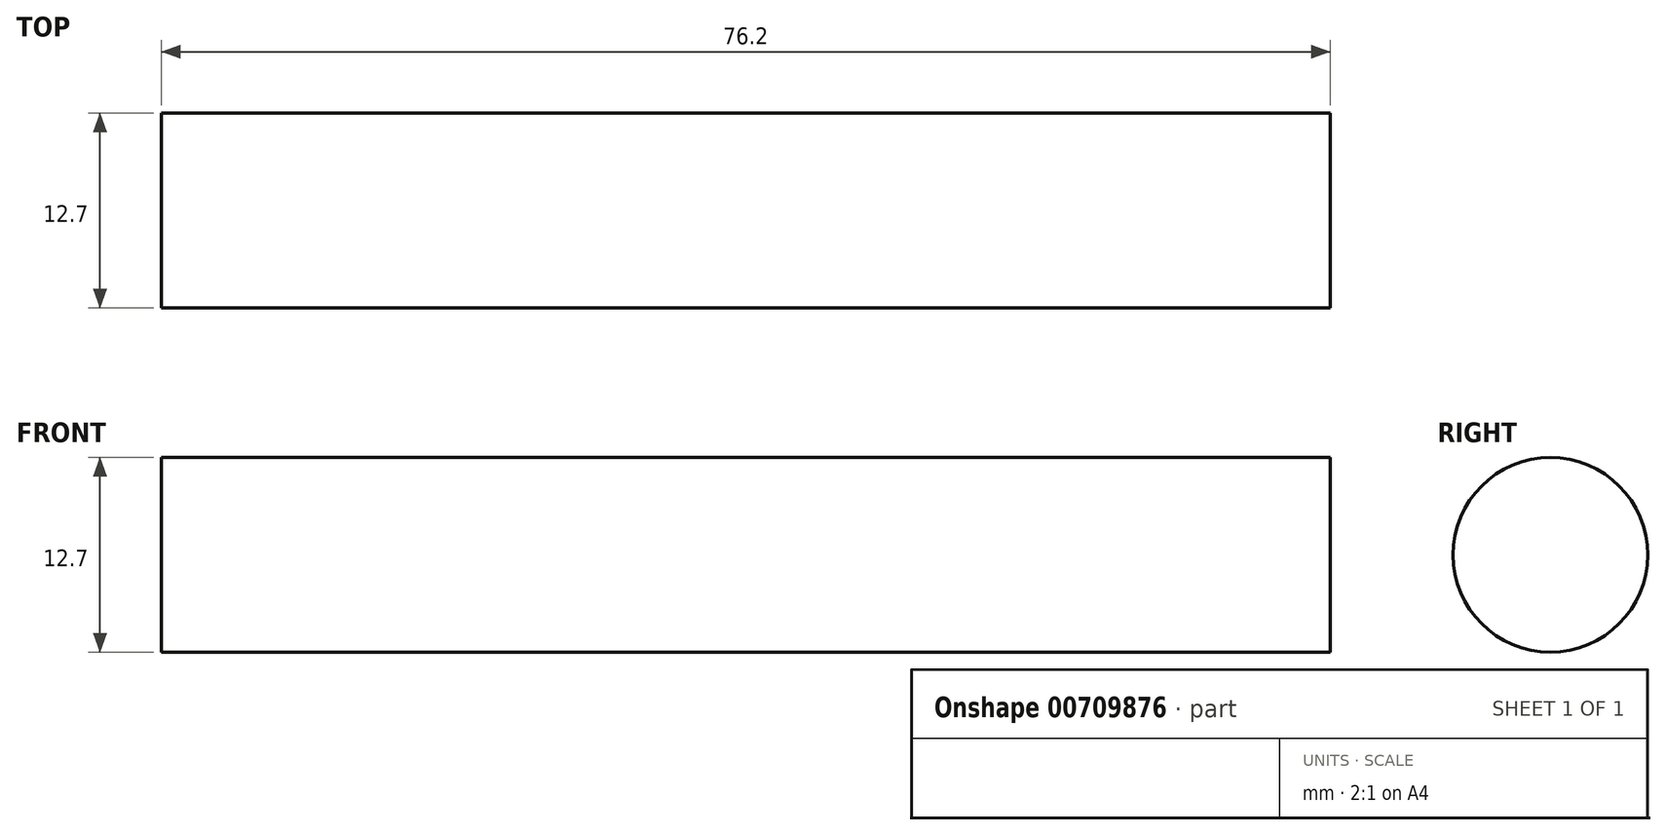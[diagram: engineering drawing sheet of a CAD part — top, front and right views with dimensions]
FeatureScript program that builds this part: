
annotation { "Feature Type Name" : "Feature", "Feature Type Description" : "" }
export const myFeature = defineFeature(function(context is Context, id is Id, definition is map)
    precondition{}
    {
        {
            var Q0;
            Q0=qCreatedBy(makeId("Right.planeOp"),FACE);
            var sketch = newSketch(context, id + "F0", { "sketchPlane" : qUnion([Q0])});
            skCircle(sketch, "E0", {"center": v(0, 0) * mm, "radius": 6.35 * mm});
            skSolve(sketch);
        }
        {
            var Q0;
            Q0 = qSketchRegion(id + "F0", true);
            extrude(context, id + "F1", {"entities" : qUnion([Q0]), "endBound" : BoundingType.SYMMETRIC, "depth" : 76.2 * mm, "offsetDistance" : 25.4 * mm});
        }
    });
